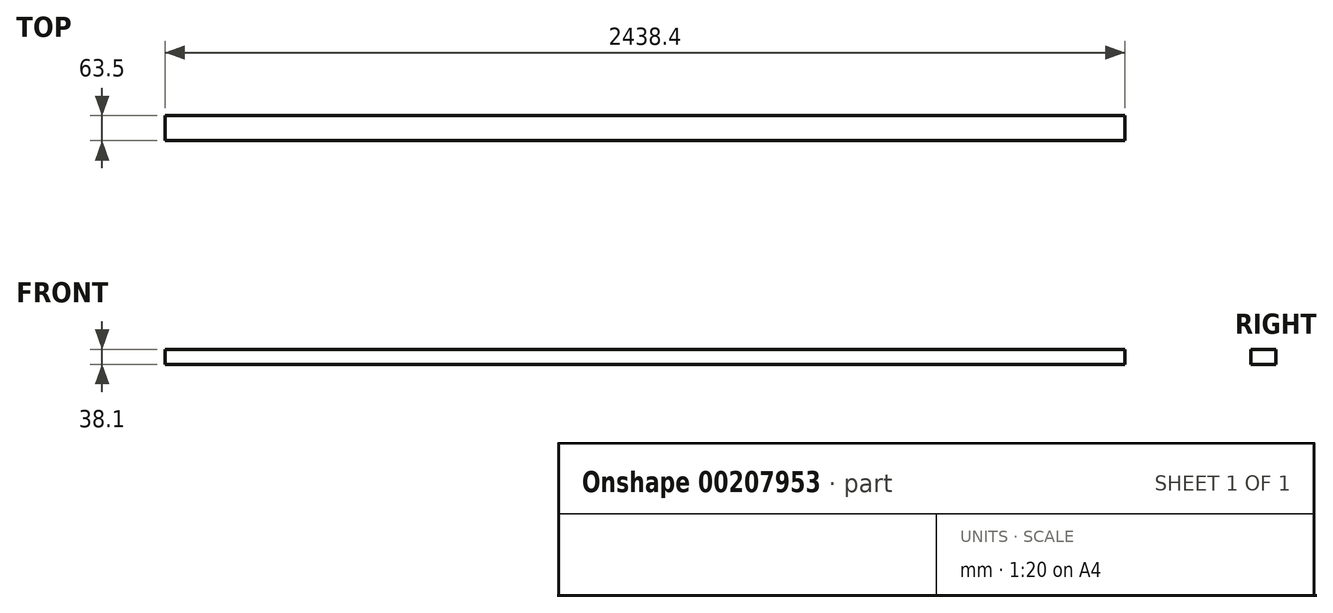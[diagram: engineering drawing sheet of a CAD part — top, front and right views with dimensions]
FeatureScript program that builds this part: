
annotation { "Feature Type Name" : "Feature", "Feature Type Description" : "" }
export const myFeature = defineFeature(function(context is Context, id is Id, definition is map)
    precondition{}
    {
        {
            var Q0;
            Q0=qCreatedBy(makeId("Right.planeOp"),FACE);
            var sketch = newSketch(context, id + "F0", { "sketchPlane" : qUnion([Q0])});
            skLineSegment(sketch, "E0.bottom", {"start": v(0, 0) * mm, "end": v(63.5, 0) * mm});
            skLineSegment(sketch, "E0.top", {"start": v(0, 38.1) * mm, "end": v(63.5, 38.1) * mm});
            skLineSegment(sketch, "E0.left", {"start": v(0, 0) * mm, "end": v(0, 38.1) * mm});
            skLineSegment(sketch, "E0.right", {"start": v(63.5, 0) * mm, "end": v(63.5, 38.1) * mm});
            skSolve(sketch);
        }
        {
            var Q0;
            Q0 = qSketchRegion(id + "F0", true);
            extrude(context, id + "F1", {"entities" : qUnion([Q0]), "depth" : 2438.4 * mm});
        }
    });
